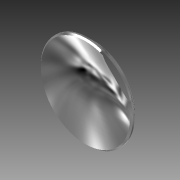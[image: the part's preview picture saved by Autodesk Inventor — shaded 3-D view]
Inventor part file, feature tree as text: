
AUTODESK INVENTOR PART (.ipt)
format: ipt  version: 2014 (Build 180170000, 170)  size: 109,056 bytes
history: native  units: mm (DEFAULTED — no unit token found)
features: sketch x3, plane x3, extrude x2, chamfer x2, reference x2
ambient origin geometry x8: Origin, YZ Plane, XZ Plane, XY Plane, X Axis, Y Axis, Z Axis, Center Point
bodies: Solid1 (feature_tree)
feature tree (12):
  sketch  "Sketch1"  dims[d2=25.4mm d3=0.0mm d4=0.127mm d5=0.127mm d6=25.4mm d7=0.0mm]
  plane  "Work Plane1"
  plane  "Work Plane2"
  extrude  "Extrusion1"  Depth=0.127mm
  chamfer  "Chamfer1"  Distance=25.4mm
  plane  "Work Plane3"
  extrude  "Extrusion2"  TaperAngle=45.0deg  [1 undecoded]
  chamfer  "Chamfer2"  [1 undecoded]
  sketch  "Sketch2"  dims[d8=0.127mm d9=0.127mm d10=45.0deg d11=45.0deg]
  reference  "Reference1"
  sketch  "Sketch3"
  reference  "Reference2"
note: 2 required parameter values undecoded (feature->parameter linkage not recoverable at this tier; creation-order binding heuristic only, values carry confidence <= 0.55)
